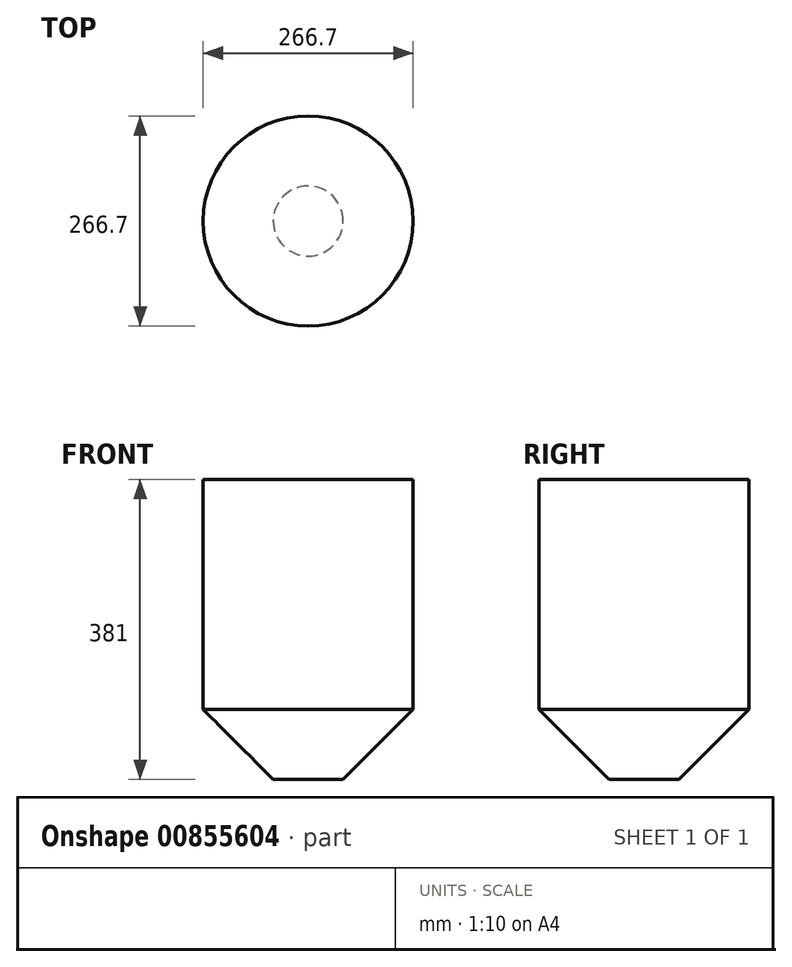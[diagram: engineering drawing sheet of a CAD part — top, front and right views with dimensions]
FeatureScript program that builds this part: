
annotation { "Feature Type Name" : "Feature", "Feature Type Description" : "" }
export const myFeature = defineFeature(function(context is Context, id is Id, definition is map)
    precondition{}
    {
        {
            var Q0;
            Q0=qCreatedBy(makeId("Front.planeOp"),FACE);
            var sketch = newSketch(context, id + "F0", { "sketchPlane" : qUnion([Q0])});
            skLineSegment(sketch, "E0", {"start": v(-66.77, 194.85) * mm, "end": v(-66.77, -97.25) * mm});
            skLineSegment(sketch, "E1", {"start": v(-66.77, -97.25) * mm, "end": v(22.13, -186.15) * mm});
            skLineSegment(sketch, "E2", {"start": v(-66.77, 194.85) * mm, "end": v(66.58, 194.85) * mm});
            skLineSegment(sketch, "E3", {"start": v(-66.77, -97.25) * mm, "end": v(-66.77, -186.15) * mm, "construction": true});
            skLineSegment(sketch, "E4", {"start": v(22.13, -186.15) * mm, "end": v(-66.77, -186.15) * mm, "construction": true});
            skLineSegment(sketch, "E5", {"start": v(66.58, 194.85) * mm, "end": v(66.58, 307.29) * mm, "construction": true});
            skLineSegment(sketch, "E6", {"start": v(66.58, 194.85) * mm, "end": v(66.58, -186.15) * mm});
            skLineSegment(sketch, "E7", {"start": v(66.58, -186.15) * mm, "end": v(22.13, -186.15) * mm});
            skSolve(sketch);
        }
        {
            var Q0;
            Q0 = qSketchRegion(id + "F0", true);
            var Q1;
            Q1=sQuery(id+"F0.wireOp",EDGE,"E5");
            revolve(context, id + "F1", {"surfaceOperationType" : NewSurfaceOperationType.NEW, "entities" : qUnion([Q0]), "axis" : qUnion([Q1]), "revolveType" : RevolveType.FULL});
        }
    });
